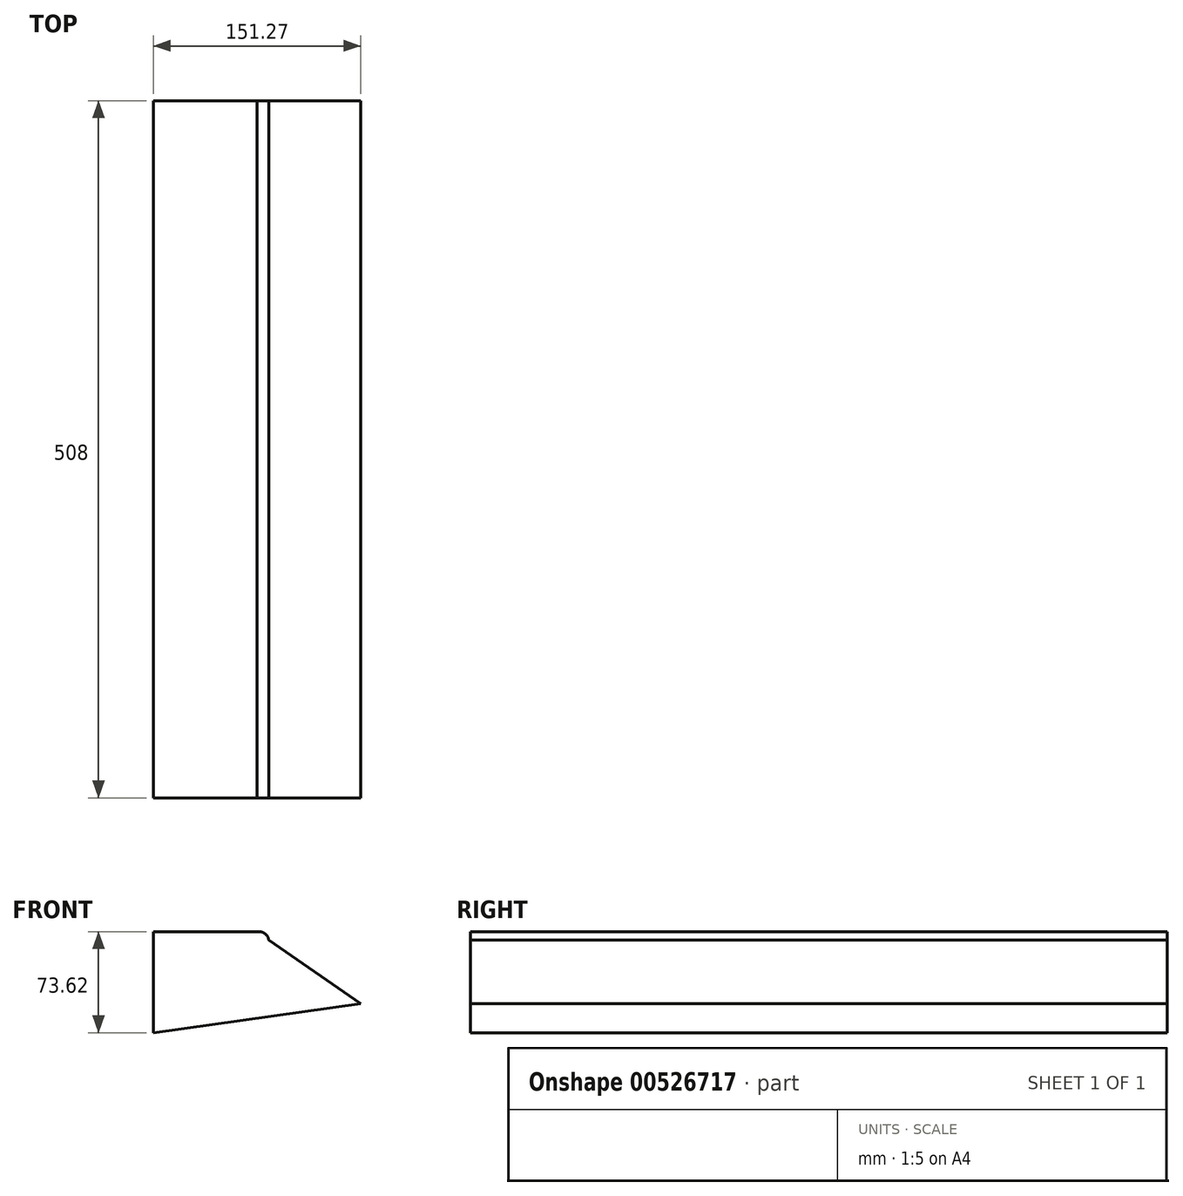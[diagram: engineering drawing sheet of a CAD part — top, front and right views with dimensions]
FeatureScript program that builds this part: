
annotation { "Feature Type Name" : "Feature", "Feature Type Description" : "" }
export const myFeature = defineFeature(function(context is Context, id is Id, definition is map)
    precondition{}
    {
        {
            var Q0;
            Q0=qCreatedBy(makeId("Front.planeOp"),FACE);
            var sketch = newSketch(context, id + "F0", { "sketchPlane" : qUnion([Q0])});
            skLineSegment(sketch, "E0", {"start": v(-75.5, 38.33) * mm, "end": v(0, 38.33) * mm});
            skLineSegment(sketch, "E1", {"start": v(0, 38.33) * mm, "end": v(75.78, -13.85) * mm});
            skLineSegment(sketch, "E2", {"start": v(-75.5, 38.33) * mm, "end": v(-75.5, -35.12) * mm});
            skLineSegment(sketch, "E3", {"start": v(-75.5, -35.12) * mm, "end": v(75.78, -13.85) * mm});
            skLineSegment(sketch, "E4", {"start": v(-762, 53.78) * mm, "end": v(0, 53.78) * mm});
            skLineSegment(sketch, "E5", {"start": v(10.2, 47.07) * mm, "end": v(1065.43, -659.6) * mm});
            skArc(sketch, "E6", {"start": v(-81.33, -25.8) * mm, "mid": v(-66.82, -22) * mm, "end": v(-63.86, -36.7) * mm});
            skArc(sketch, "E7", {"start": v(66.46, 0) * mm, "mid": v(44.24, -6.2) * mm, "end": v(46.73, -29.14) * mm});
            skArc(sketch, "E8", {"start": v(-5.54, 32.2) * mm, "mid": v(6.85, 26.56) * mm, "end": v(0, 38.33) * mm});
            skSolve(sketch);
        }
        {
            var Q0;
            Q0 = qSketchRegion(id + "F0", true);
            extrude(context, id + "F1", {"entities" : qUnion([Q0]), "depth" : 508 * mm, "offsetDistance" : 25.4 * mm});
        }
    });
